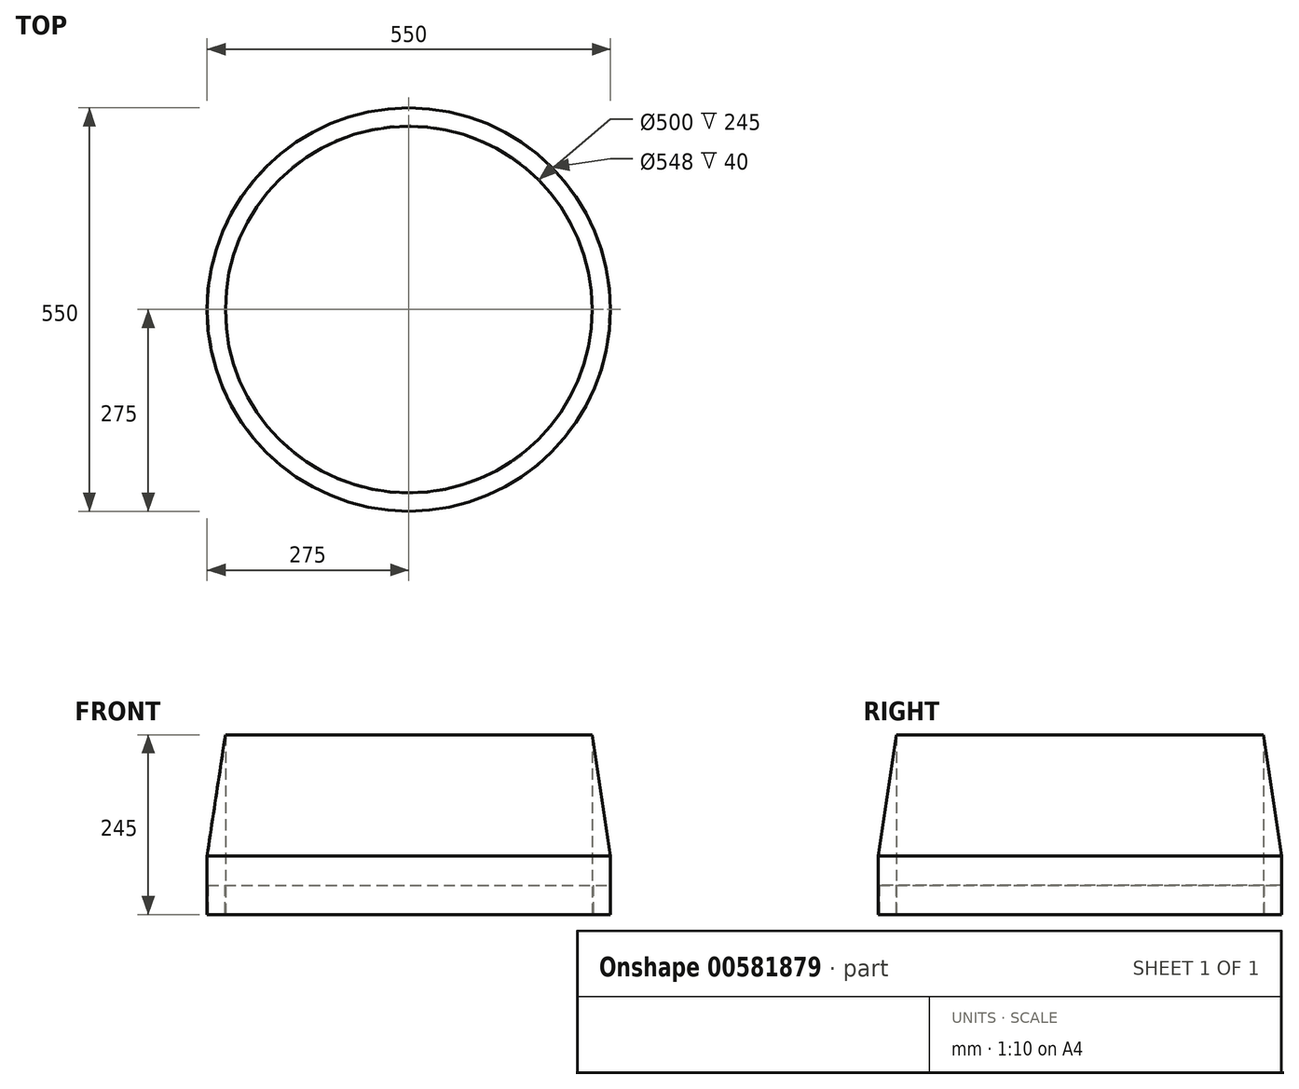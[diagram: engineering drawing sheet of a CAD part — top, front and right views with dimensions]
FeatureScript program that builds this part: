
annotation { "Feature Type Name" : "Feature", "Feature Type Description" : "" }
export const myFeature = defineFeature(function(context is Context, id is Id, definition is map)
    precondition{}
    {
        {
            var Q0;
            Q0=qCreatedBy(makeId("Front.planeOp"),FACE);
            var sketch = newSketch(context, id + "F0", { "sketchPlane" : qUnion([Q0])});
            skLineSegment(sketch, "E0", {"start": v(0, -139.25) * mm, "end": v(0, 240.83) * mm, "construction": true});
            skLineSegment(sketch, "E1", {"start": v(-250, -67.22) * mm, "end": v(-250, 177.78) * mm});
            skLineSegment(sketch, "E2", {"start": v(-250, 177.78) * mm, "end": v(-275, 12.78) * mm});
            skLineSegment(sketch, "E3", {"start": v(-275, 12.78) * mm, "end": v(-275, -67.22) * mm});
            skLineSegment(sketch, "E4", {"start": v(-275, -67.22) * mm, "end": v(-274, -67.22) * mm});
            skLineSegment(sketch, "E5", {"start": v(-274, -67.22) * mm, "end": v(-274, -27.22) * mm});
            skLineSegment(sketch, "E6", {"start": v(-274, -27.22) * mm, "end": v(-251, -27.22) * mm});
            skLineSegment(sketch, "E7", {"start": v(-251, -27.22) * mm, "end": v(-251, -67.22) * mm});
            skLineSegment(sketch, "E8", {"start": v(-251, -67.22) * mm, "end": v(-250, -67.22) * mm});
            skSolve(sketch);
        }
        {
            var Q0;
            Q0=qSketchRegion(id+"F0",true);
            var Q1;
            Q1=sQuery(id+"F0.wireOp",EDGE,"E0");
            revolve(context, id + "F1", {"entities" : qUnion([Q0]), "axis" : qUnion([Q1]), "revolveType" : RevolveType.FULL});
        }
    });
